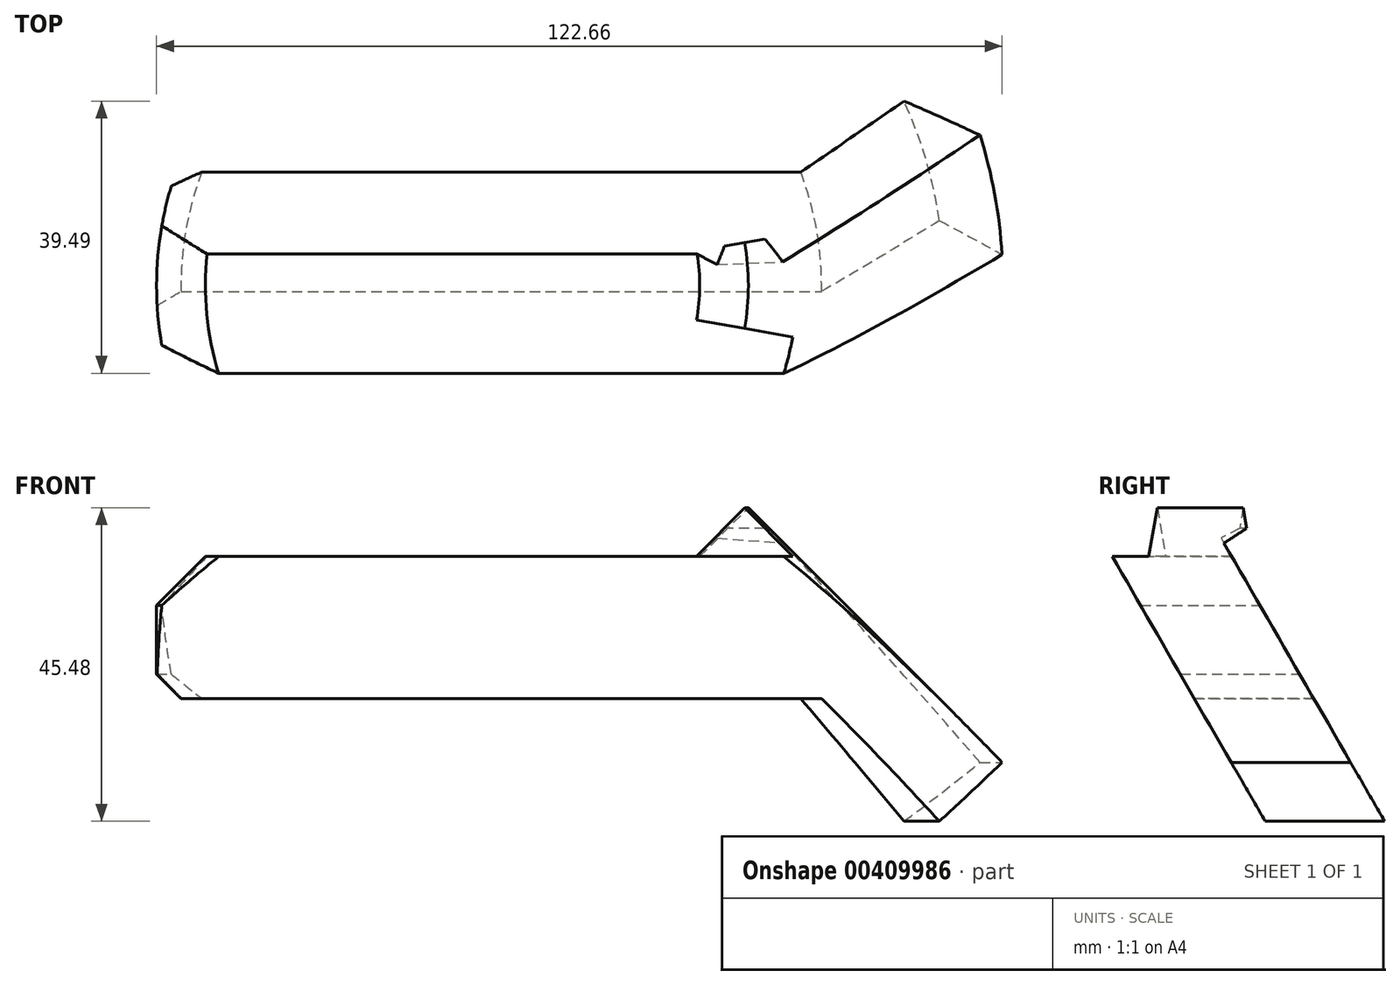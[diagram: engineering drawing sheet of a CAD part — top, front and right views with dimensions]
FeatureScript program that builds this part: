
annotation { "Feature Type Name" : "Feature", "Feature Type Description" : "" }
export const myFeature = defineFeature(function(context is Context, id is Id, definition is map)
    precondition{}
    {
        {
            var Q0;
            Q0=qCreatedBy(makeId("Front.planeOp"),FACE);
            var sketch = newSketch(context, id + "F0", { "sketchPlane" : qUnion([Q0])});
            skLineSegment(sketch, "E0", {"start": v(0, -13.54) * mm, "end": v(0, 7.07) * mm});
            skLineSegment(sketch, "E1", {"start": v(0, 7.07) * mm, "end": v(42.93, 7.07) * mm});
            skLineSegment(sketch, "E2", {"start": v(0, -13.54) * mm, "end": v(46.46, -13.54) * mm});
            skLineSegment(sketch, "E3", {"start": v(46.46, -13.54) * mm, "end": v(50, -10) * mm});
            skLineSegment(sketch, "E4", {"start": v(50, -10) * mm, "end": v(50, 0) * mm});
            skLineSegment(sketch, "E5", {"start": v(50, 0) * mm, "end": v(42.93, 7.07) * mm});
            skLineSegment(sketch, "E6", {"start": v(50, 0) * mm, "end": v(72.8, -22.8) * mm});
            skLineSegment(sketch, "E7", {"start": v(64.27, -31.34) * mm, "end": v(46.46, -13.54) * mm});
            skLineSegment(sketch, "E8", {"start": v(42.93, 7.07) * mm, "end": v(35.86, 14.14) * mm});
            skLineSegment(sketch, "E9", {"start": v(35.86, 14.14) * mm, "end": v(28.79, 7.07) * mm});
            skLineSegment(sketch, "E10", {"start": v(32.32, 10.6) * mm, "end": v(14.64, 28.28) * mm, "construction": true});
            skPoint(sketch, "E11", {"position": v(65, -23.54) * mm});
            skLineSegment(sketch, "E12", {"start": v(50, -17.07) * mm, "end": v(32.32, -34.75) * mm, "construction": true});
            skLineSegment(sketch, "E13", {"start": v(55, -5) * mm, "end": v(72.68, 12.68) * mm, "construction": true});
            skLineSegment(sketch, "E14", {"start": v(64.27, -31.34) * mm, "end": v(72.8, -22.8) * mm});
            skLineSegment(sketch, "E15", {"start": v(68.54, -27.07) * mm, "end": v(86.21, -44.75) * mm, "construction": true});
            skLineSegment(sketch, "E16", {"start": v(50, -5) * mm, "end": v(75, -5) * mm, "construction": true});
            skSolve(sketch);
        }
        {
            var Q0;
            Q0=makeQuery(id+"F0.imprint","IMPRINT",FACE,{"disambiguationData":[TD([[makeQuery(id+"F0.imprint","IMPRINT",EDGE,{"derivedFrom":sQuery(id+"F0.wireOp",EDGE,"E0")}),-1.0]])]});
            var Q1;
            Q1=sQuery(id+"F0.wireOp",EDGE,"E0");
            revolve(context, id + "F1", {"entities" : qUnion([Q0]), "axis" : qUnion([Q1]), "revolveType" : RevolveType.FULL});
        }
        {
            var Q0;
            Q0=makeQuery(id+"F0.imprint","IMPRINT",FACE,{"disambiguationData":[TD([[makeQuery(id+"F0.imprint","IMPRINT",EDGE,{"derivedFrom":sQuery(id+"F0.wireOp",EDGE,"E3")}),-1.0]])]});
            var Q1;
            Q1=sQuery(id+"F0.wireOp",EDGE,"E0");
            revolve(context, id + "F2", {"entities" : qUnion([Q0]), "axis" : qUnion([Q1]), "revolveType" : RevolveType.SYMMETRIC, "angle" : 180 * degree});
        }
        {
            var Q0;
            Q0=qCreatedBy(makeId("Right.planeOp"),FACE);
            var sketch = newSketch(context, id + "F3", { "sketchPlane" : qUnion([Q0])});
            skLineSegment(sketch, "E17", {"start": v(0, 0) * mm, "end": v(25.98, 15) * mm, "construction": true});
            skSolve(sketch);
        }
        {
            var Q0;
            Q0=sQuery(id+"F3.wireOp",EDGE,"E17");
            var Q1;
            Q1=sQuery(id+"F3.wireOp",VERTEX,"E17.start");
            cPlane(context, id + "F4", {"entities" : qUnion([Q0, Q1]), "cplaneType" : CPlaneType.LINE_POINT, "offset" : 25 * mm, "width" : 150 * mm, "height" : 150 * mm});
        }
        {
            var Q0;
            Q0=qCreatedBy(id+"F4.planeOp",FACE);
            var sketch = newSketch(context, id + "F5", { "sketchPlane" : qUnion([Q0])});
            skCircle(sketch, "E18", {"center": v(0, 0) * mm, "radius": 85.43 * mm});
            skSolve(sketch);
        }
        {
            var Q0;
            Q0=qSketchRegion(id+"F5",true);
            extrude(context, id + "F6", {"entities" : qUnion([Q0]), "operationType" : NewBodyOperationType.INTERSECT, "endBound" : BoundingType.SYMMETRIC, "depth" : 15 * mm});
        }
        {
            var Q0;
            Q0=makeQuery(id+"F1.opRevolve","SWEPT_BODY",BODY,{"disambiguationData":[OSD([sQuery(id+"F0.wireOp",EDGE,"E0"),sQuery(id+"F0.wireOp",EDGE,"E1"),sQuery(id+"F0.wireOp",EDGE,"E2"),sQuery(id+"F0.wireOp",EDGE,"E3"),sQuery(id+"F0.wireOp",EDGE,"E4"),sQuery(id+"F0.wireOp",EDGE,"E5")])]});
            var Q1;
            Q1=makeQuery(id+"F2.opRevolve","SWEPT_BODY",BODY,{"disambiguationData":[OSD([sQuery(id+"F0.wireOp",EDGE,"E3"),sQuery(id+"F0.wireOp",EDGE,"E4"),sQuery(id+"F0.wireOp",EDGE,"E6"),sQuery(id+"F0.wireOp",EDGE,"E7"),sQuery(id+"F0.wireOp",EDGE,"E14")])]});
            booleanBodies(context, id + "F7", {"operationType" : BooleanOperationType.UNION, "tools" : qUnion([Q0, Q1])});
        }
        {
            var Q0;
            {var subQ0=sQuery(id+"F0.wireOp",EDGE,"E8");Q0=makeQuery(id+"F0.imprint","IMPRINT",FACE,{"disambiguationData":[TD([[makeQuery(id+"F0.imprint","IMPRINT",EDGE,{"derivedFrom":subQ0}),1.0]])]});}
            var Q1;
            Q1=sQuery(id+"F0.wireOp",EDGE,"E0");
            revolve(context, id + "F8", {"operationType" : NewBodyOperationType.ADD, "entities" : qUnion([Q0]), "axis" : qUnion([Q1]), "revolveType" : RevolveType.SYMMETRIC, "angle" : 20 * degree});
        }
        {
            var Q0;
            Q0=makeQuery(id+"F8.opRevolve","CAP_EDGE",EDGE,{"disambiguationData":[OSD([sQuery(id+"F0.wireOp",EDGE,"E1")])],"isStart":true});
            var Q1;
            Q1=makeQuery(id+"F8.opRevolve","CAP_EDGE",EDGE,{"disambiguationData":[OSD([sQuery(id+"F0.wireOp",EDGE,"E1")])],"isStart":false});
            chamfer(context, id + "F9", {"entities" : qUnion([Q0, Q1]), "chamferType" : ChamferType.OFFSET_ANGLE, "width" : 7.07 * mm, "oppositeDirection" : false, "angle" : 30 * degree, "tangentPropagation" : true});
        }
    });
